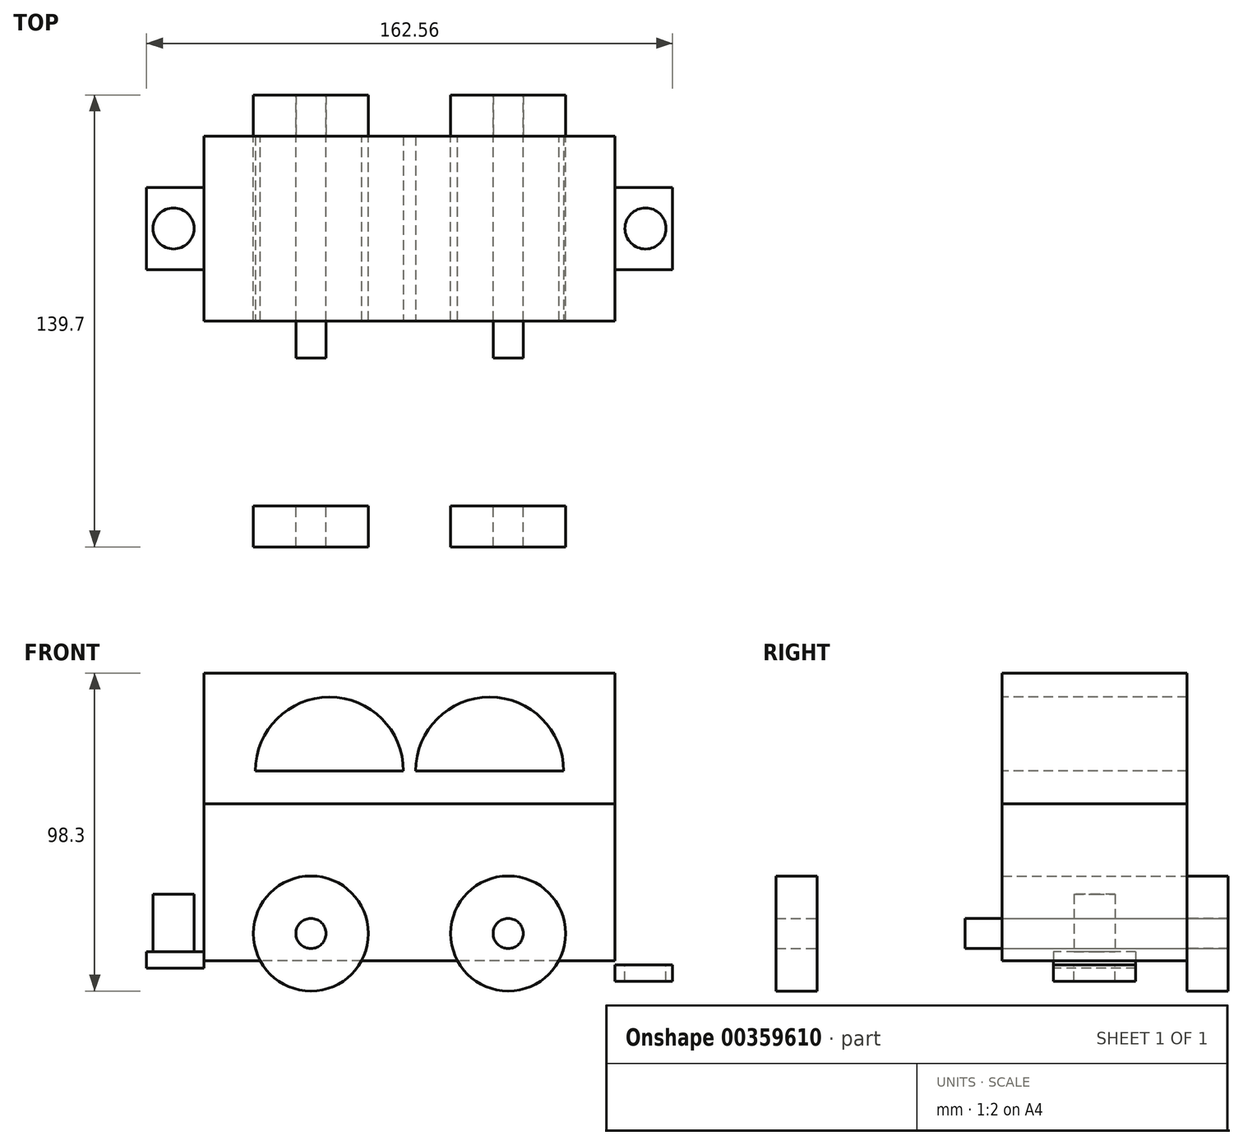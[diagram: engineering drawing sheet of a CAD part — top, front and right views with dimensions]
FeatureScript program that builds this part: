
annotation { "Feature Type Name" : "Feature", "Feature Type Description" : "" }
export const myFeature = defineFeature(function(context is Context, id is Id, definition is map)
    precondition{}
    {
        {
            var Q0;
            Q0=qCreatedBy(makeId("Front.planeOp"),FACE);
            var sketch = newSketch(context, id + "F0", { "sketchPlane" : qUnion([Q0])});
            skLineSegment(sketch, "E0.bottom", {"start": v(0, 0) * mm, "end": v(-127, 0) * mm});
            skLineSegment(sketch, "E0.top", {"start": v(0, -88.9) * mm, "end": v(-127, -88.9) * mm});
            skLineSegment(sketch, "E0.left", {"start": v(0, 0) * mm, "end": v(0, -88.9) * mm});
            skLineSegment(sketch, "E0.right", {"start": v(-127, 0) * mm, "end": v(-127, -88.9) * mm});
            skCircle(sketch, "E1", {"center": v(-93.98, -80.52) * mm, "radius": 17.78 * mm});
            skCircle(sketch, "E2", {"center": v(-33.02, -80.52) * mm, "radius": 17.78 * mm});
            skLineSegment(sketch, "E3.bottom", {"start": v(-127, -40.44) * mm, "end": v(0, -40.44) * mm});
            skLineSegment(sketch, "E3.top", {"start": v(-127, -31.32) * mm, "end": v(0, -31.32) * mm});
            skLineSegment(sketch, "E3.left", {"start": v(-127, -31.32) * mm, "end": v(-127, -40.44) * mm});
            skLineSegment(sketch, "E3.right", {"start": v(0, -31.32) * mm, "end": v(0, -40.44) * mm});
            skCircle(sketch, "E4", {"center": v(-93.98, -80.52) * mm, "radius": 4.65 * mm});
            skCircle(sketch, "E5", {"center": v(-33.02, -80.52) * mm, "radius": 4.65 * mm});
            skSolve(sketch);
        }
        {
            var Q0;
            {var subQ0=sQuery(id+"F0.wireOp",EDGE,"E0.bottom");Q0=makeQuery(id+"F0.imprint","IMPRINT",FACE,{"disambiguationData":[TD([[makeQuery(id+"F0.imprint","IMPRINT",EDGE,{"derivedFrom":subQ0}),1.0]])]});}
            var Q1;
            {var subQ3=sQuery(id+"F0.wireOp",EDGE,"E3.top");Q1=makeQuery(id+"F0.imprint","IMPRINT",FACE,{"disambiguationData":[TD([[makeQuery(id+"F0.imprint","IMPRINT",EDGE,{"derivedFrom":subQ3}),-1.0]])]});}
            var Q2;
            Q2=makeQuery(id+"F0.imprint","IMPRINT",FACE,{"disambiguationData":[TD([[makeQuery(id+"F0.imprint","IMPRINT",EDGE,{"derivedFrom":sQuery(id+"F0.wireOp",EDGE,"E5")}),-1.0]])]});
            var Q3;
            Q3=makeQuery(id+"F0.imprint","IMPRINT",FACE,{"disambiguationData":[TD([[makeQuery(id+"F0.imprint","IMPRINT",EDGE,{"derivedFrom":sQuery(id+"F0.wireOp",EDGE,"E4")}),-1.0]])]});
            extrude(context, id + "F1", {"entities" : qUnion([Q0, Q1, Q2, Q3]), "depth" : 57.15 * mm});
        }
        {
            var Q0;
            Q0=makeQuery(id+"F0.imprint","IMPRINT",FACE,{"disambiguationData":[TD([[makeQuery(id+"F0.imprint","IMPRINT",EDGE,{"derivedFrom":sQuery(id+"F0.wireOp",EDGE,"E3.bottom")}),-1.0]])]});
            extrude(context, id + "F2", {"entities" : qUnion([Q0]), "depth" : 57.15 * mm});
        }
        {
            var Q0;
            {var subQ0=sQuery(id+"F0.wireOp",EDGE,"E2");var subQ1=sQuery(id+"F0.wireOp",EDGE,"E0.top");var subQ2=makeQuery(id+"F0.imprint","INTERSECT",VERTEX,{"disambiguationData":[OD(0.0)],"derivedFrom":[subQ1,subQ0]});Q0=makeQuery(id+"F0.imprint","IMPRINT",FACE,{"disambiguationData":[TD([[makeQuery(id+"F0.imprint","IMPRINT",EDGE,{"disambiguationData":[TD([[subQ2,-1.0]])],"derivedFrom":subQ1}),1.0]])]});}
            var Q1;
            Q1=makeQuery(id+"F0.imprint","IMPRINT",FACE,{"disambiguationData":[TD([[makeQuery(id+"F0.imprint","IMPRINT",EDGE,{"derivedFrom":sQuery(id+"F0.wireOp",EDGE,"E5")}),-1.0]])]});
            var Q2;
            Q2=makeQuery(id+"F0.imprint","IMPRINT",FACE,{"disambiguationData":[TD([[makeQuery(id+"F0.imprint","IMPRINT",EDGE,{"derivedFrom":sQuery(id+"F0.wireOp",EDGE,"E4")}),-1.0]])]});
            var Q3;
            {var subQ0=sQuery(id+"F0.wireOp",EDGE,"E1");var subQ1=sQuery(id+"F0.wireOp",EDGE,"E0.top");var subQ2=makeQuery(id+"F0.imprint","INTERSECT",VERTEX,{"disambiguationData":[OD(0.0)],"derivedFrom":[subQ1,subQ0]});Q3=makeQuery(id+"F0.imprint","IMPRINT",FACE,{"disambiguationData":[TD([[makeQuery(id+"F0.imprint","IMPRINT",EDGE,{"disambiguationData":[TD([[subQ2,-1.0]])],"derivedFrom":subQ1}),1.0]])]});}
            extrude(context, id + "F3", {"entities" : qUnion([Q0, Q1, Q2, Q3]), "oppositeDirection" : true, "depth" : 12.7 * mm});
        }
        {
            var Q0;
            Q0=makeQuery(id+"F3.opExtrude","SWEPT_BODY",BODY,{"disambiguationData":[OSD([sQuery(id+"F0.wireOp",EDGE,"E2"),sQuery(id+"F0.wireOp",EDGE,"E5")])]});
            var Q1;
            Q1=makeQuery(id+"F3.opExtrude","SWEPT_BODY",BODY,{"disambiguationData":[OSD([sQuery(id+"F0.wireOp",EDGE,"E1"),sQuery(id+"F0.wireOp",EDGE,"E4")])]});
            var Q2;
            Q2=makeQuery(id+"F1.opExtrude","CAP_FACE",FACE,{"disambiguationData":[OSD([sQuery(id+"F0.wireOp",EDGE,"E0.top"),sQuery(id+"F0.wireOp",EDGE,"E0.left"),sQuery(id+"F0.wireOp",EDGE,"E0.right"),sQuery(id+"F0.wireOp",EDGE,"E1"),sQuery(id+"F0.wireOp",EDGE,"E2"),sQuery(id+"F0.wireOp",EDGE,"E3.top")])],"isStart":false});
            mirror(context, id + "F4", {"entities" : qUnion([Q0, Q1]), "mirrorPlane" : qUnion([Q2])});
        }
        {
            var Q0;
            {var subQ0=sQuery(id+"F0.wireOp",EDGE,"E0.right");Q0=makeQuery(id+"F1.opExtrude","SWEPT_FACE",FACE,{"disambiguationData":[OSD([subQ0]),TDD([makeQuery(id+"F0.imprint","IMPRINT",EDGE,{"disambiguationData":[TD([[makeQuery(id+"F0.imprint","INTERSECT",VERTEX,{"derivedFrom":[sQuery(id+"F0.wireOp",EDGE,"E0.top"),subQ0]}),1.0]])],"derivedFrom":subQ0})])]});}
            var sketch = newSketch(context, id + "F5", { "sketchPlane" : qUnion([Q0])});
            skLineSegment(sketch, "E6.bottom", {"start": v(15.88, -86.16) * mm, "end": v(41.28, -86.16) * mm});
            skLineSegment(sketch, "E6.top", {"start": v(15.88, -91.24) * mm, "end": v(41.28, -91.24) * mm});
            skLineSegment(sketch, "E6.left", {"start": v(15.88, -86.16) * mm, "end": v(15.88, -91.24) * mm});
            skLineSegment(sketch, "E6.right", {"start": v(41.28, -86.16) * mm, "end": v(41.28, -91.24) * mm});
            skSolve(sketch);
        }
        {
            var Q0;
            Q0 = qSketchRegion(id + "F5", true);
            extrude(context, id + "F6", {"entities" : qUnion([Q0]), "operationType" : NewBodyOperationType.ADD, "depth" : 17.78 * mm});
        }
        {
            var Q0;
            Q0=makeQuery(id+"F6.opExtrude","SWEPT_FACE",FACE,{"disambiguationData":[OSD([sQuery(id+"F5.wireOp",EDGE,"E6.bottom")])]});
            var sketch = newSketch(context, id + "F7", { "sketchPlane" : qUnion([Q0])});
            skCircle(sketch, "E7", {"center": v(-136.43, -28.58) * mm, "radius": 6.35 * mm});
            skPoint(sketch, "E7.centerSnap0", {"position": v(-144.78, -28.58) * mm});
            skSolve(sketch);
        }
        {
            var Q0;
            Q0 = qSketchRegion(id + "F7", true);
            extrude(context, id + "F8", {"entities" : qUnion([Q0]), "operationType" : NewBodyOperationType.ADD, "depth" : 17.78 * mm});
        }
        {
            var Q0;
            Q0=makeQuery(id+"F0.imprint","IMPRINT",FACE,{"disambiguationData":[TD([[makeQuery(id+"F0.imprint","IMPRINT",EDGE,{"derivedFrom":sQuery(id+"F0.wireOp",EDGE,"E5")}),1.0]])]});
            var Q1;
            Q1=makeQuery(id+"F0.imprint","IMPRINT",FACE,{"disambiguationData":[TD([[makeQuery(id+"F0.imprint","IMPRINT",EDGE,{"derivedFrom":sQuery(id+"F0.wireOp",EDGE,"E4")}),1.0]])]});
            extrude(context, id + "F9", {"entities" : qUnion([Q0, Q1]), "depth" : 68.58 * mm, "hasSecondDirection" : true, "secondDirectionOppositeDirection" : true, "secondDirectionDepth" : 12.7 * mm});
        }
        {
            var Q0;
            {var subQ0=sQuery(id+"F0.wireOp",EDGE,"E0.left");Q0=makeQuery(id+"F1.opExtrude","SWEPT_FACE",FACE,{"disambiguationData":[OSD([subQ0]),TDD([makeQuery(id+"F0.imprint","IMPRINT",EDGE,{"disambiguationData":[TD([[makeQuery(id+"F0.imprint","INTERSECT",VERTEX,{"derivedFrom":[sQuery(id+"F0.wireOp",EDGE,"E0.top"),subQ0]}),1.0]])],"derivedFrom":subQ0})])]});}
            var sketch = newSketch(context, id + "F10", { "sketchPlane" : qUnion([Q0])});
            skSolve(sketch);
        }
        {
            var Q0;
            {var subQ0=sQuery(id+"F0.wireOp",EDGE,"E0.left");var subQ1=sQuery(id+"F0.wireOp",EDGE,"E0.top");Q0=makeQuery(id+"F10.imprint","IMPRINT",FACE,{"disambiguationData":[TD([[makeQuery(id+"F10.imprint","IMPRINT",EDGE,{"derivedFrom":makeQuery(id+"F1.opExtrude","SWEPT_EDGE",EDGE,{"disambiguationData":[OSD([subQ1,subQ0])]})}),1.0]])]});}
            var sketch = newSketch(context, id + "F11", { "sketchPlane" : qUnion([Q0])});
            skLineSegment(sketch, "E8.bottom", {"start": v(-41.28, -95.28) * mm, "end": v(-15.88, -95.28) * mm});
            skLineSegment(sketch, "E8.top", {"start": v(-41.28, -90.2) * mm, "end": v(-15.88, -90.2) * mm});
            skLineSegment(sketch, "E8.left", {"start": v(-41.28, -90.2) * mm, "end": v(-41.28, -95.28) * mm});
            skLineSegment(sketch, "E8.right", {"start": v(-15.88, -90.2) * mm, "end": v(-15.88, -95.28) * mm});
            skSolve(sketch);
        }
        {
            var Q0;
            Q0 = qSketchRegion(id + "F11", true);
            extrude(context, id + "F12", {"entities" : qUnion([Q0]), "operationType" : NewBodyOperationType.ADD, "depth" : 17.78 * mm});
        }
        {
            var Q0;
            Q0=makeQuery(id+"F12.opExtrude","SWEPT_FACE",FACE,{"disambiguationData":[OSD([sQuery(id+"F11.wireOp",EDGE,"E8.top")])]});
            var sketch = newSketch(context, id + "F13", { "sketchPlane" : qUnion([Q0])});
            skCircle(sketch, "E9", {"center": v(9.42, -28.59) * mm, "radius": 6.35 * mm});
            skSolve(sketch);
        }
        {
            var Q0;
            Q0 = qSketchRegion(id + "F13", true);
            extrude(context, id + "F14", {"entities" : qUnion([Q0]), "operationType" : NewBodyOperationType.REMOVE, "oppositeDirection" : true, "depth" : 25.4 * mm});
        }
        {
            var Q0;
            Q0=makeQuery(id+"F1.opExtrude","CAP_FACE",FACE,{"disambiguationData":[OSD([sQuery(id+"F0.wireOp",EDGE,"E0.bottom"),sQuery(id+"F0.wireOp",EDGE,"E0.left"),sQuery(id+"F0.wireOp",EDGE,"E0.right"),sQuery(id+"F0.wireOp",EDGE,"E3.bottom")])],"isStart":false});
            var sketch = newSketch(context, id + "F15", { "sketchPlane" : qUnion([Q0])});
            skArc(sketch, "E10", {"start": v(-65.4, -30.28) * mm, "mid": v(-88.26, -7.42) * mm, "end": v(-111.12, -30.28) * mm});
            skArc(sketch, "E11", {"start": v(-15.88, -30.28) * mm, "mid": v(-38.74, -7.42) * mm, "end": v(-61.6, -30.28) * mm});
            skLineSegment(sketch, "E12", {"start": v(-111.12, -30.28) * mm, "end": v(-65.4, -30.28) * mm});
            skLineSegment(sketch, "E13", {"start": v(-61.6, -30.28) * mm, "end": v(-15.88, -30.28) * mm});
            skSolve(sketch);
        }
        {
            var Q0;
            Q0=makeQuery(id+"F15.imprint","IMPRINT",FACE,{"disambiguationData":[TD([[makeQuery(id+"F15.imprint","IMPRINT",EDGE,{"derivedFrom":sQuery(id+"F15.wireOp",EDGE,"E10")}),1.0]])]});
            var Q1;
            Q1=makeQuery(id+"F15.imprint","IMPRINT",FACE,{"disambiguationData":[TD([[makeQuery(id+"F15.imprint","IMPRINT",EDGE,{"derivedFrom":sQuery(id+"F15.wireOp",EDGE,"E11")}),1.0]])]});
            var Q2;
            Q2=sQuery(id+"F15.wireOp",EDGE,"E12");
            var Q3;
            Q3=sQuery(id+"F15.wireOp",EDGE,"E10");
            var Q4;
            Q4=sQuery(id+"F15.wireOp",EDGE,"E11");
            var Q5;
            Q5=sQuery(id+"F15.wireOp",EDGE,"E13");
            extrude(context, id + "F16", {"entities" : qUnion([Q0, Q1]), "operationType" : NewBodyOperationType.REMOVE, "surfaceEntities" : qUnion([Q2, Q3, Q4, Q5]), "oppositeDirection" : true, "depth" : 67.82 * mm});
        }
    });
